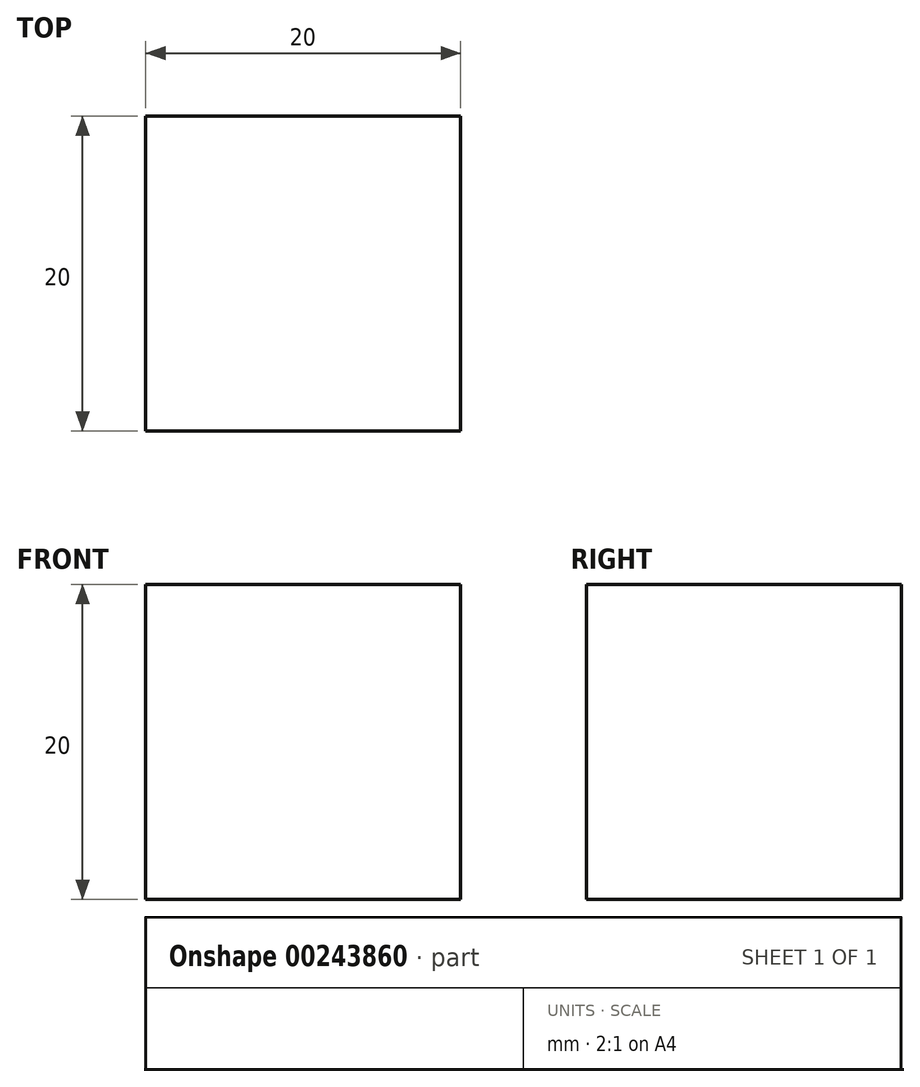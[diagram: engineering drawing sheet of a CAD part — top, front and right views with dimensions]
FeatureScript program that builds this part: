
annotation { "Feature Type Name" : "Feature", "Feature Type Description" : "" }
export const myFeature = defineFeature(function(context is Context, id is Id, definition is map)
    precondition{}
    {
        {
            var Q0;
            Q0=qCreatedBy(makeId("Top.planeOp"),FACE);
            var sketch = newSketch(context, id + "F0", { "sketchPlane" : qUnion([Q0])});
            skLineSegment(sketch, "E0.bottom", {"start": v(10, 10.48) * mm, "end": v(-10, 10.48) * mm});
            skLineSegment(sketch, "E0.top", {"start": v(10, -9.52) * mm, "end": v(-10, -9.52) * mm});
            skLineSegment(sketch, "E0.left", {"start": v(10, 10.48) * mm, "end": v(10, -9.52) * mm});
            skLineSegment(sketch, "E0.right", {"start": v(-10, 10.48) * mm, "end": v(-10, -9.52) * mm});
            skPoint(sketch, "E0.middle", {"position": v(0, 0.48) * mm});
            skSolve(sketch);
        }
        {
            var Q0;
            Q0 = qSketchRegion(id + "F0", true);
            extrude(context, id + "F1", {"entities" : qUnion([Q0]), "depth" : 20 * mm, "offsetDistance" : 25 * mm});
        }
    });
